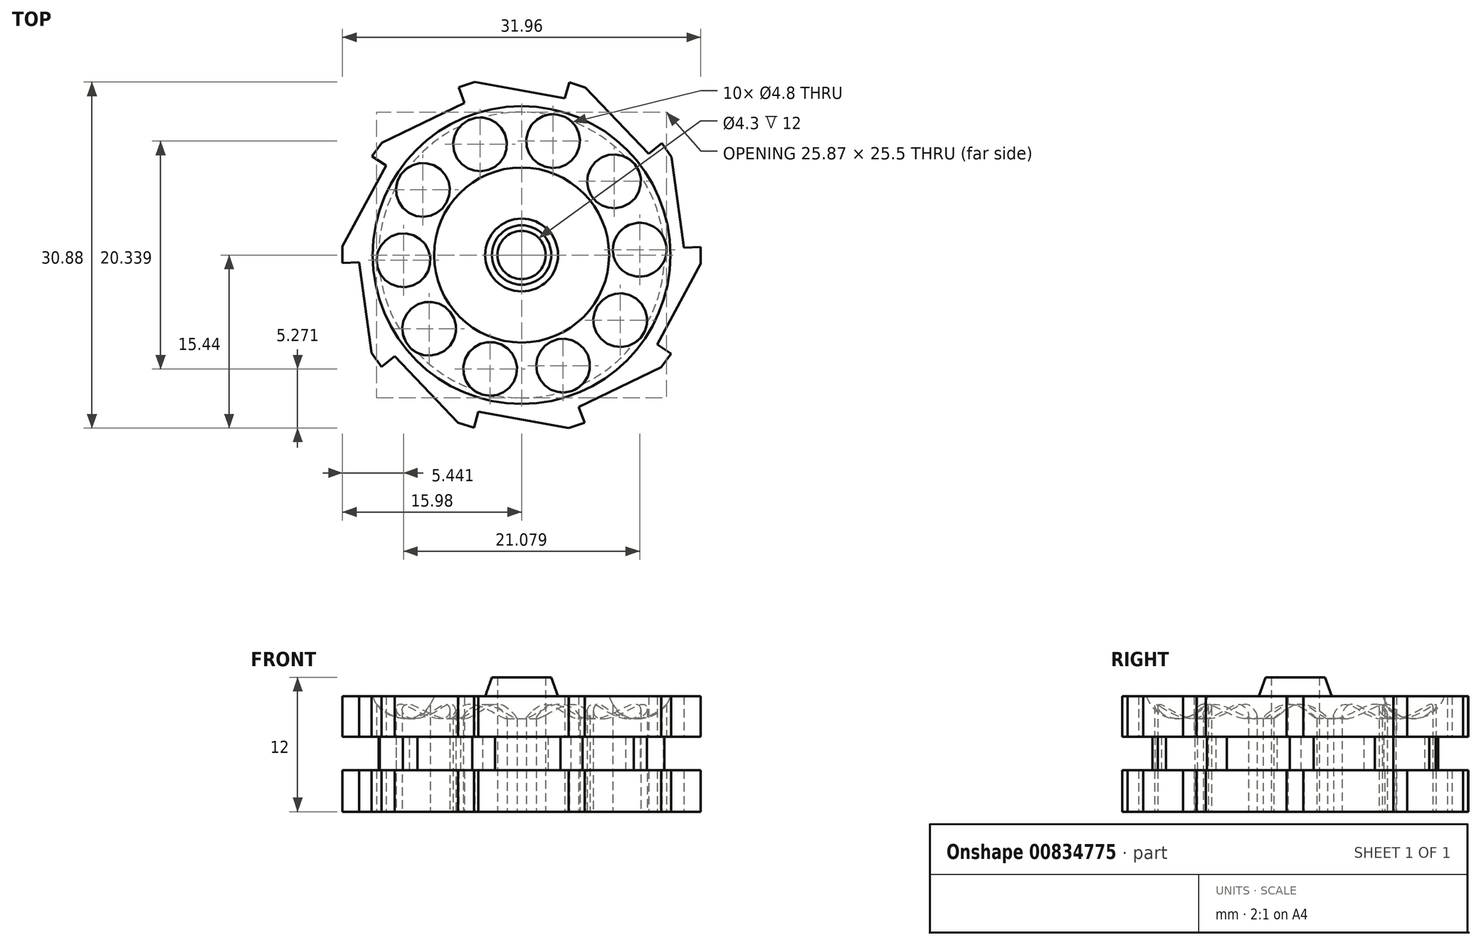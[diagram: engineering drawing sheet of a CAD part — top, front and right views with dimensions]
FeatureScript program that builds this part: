
annotation { "Feature Type Name" : "Feature", "Feature Type Description" : "" }
export const myFeature = defineFeature(function(context is Context, id is Id, definition is map)
    precondition{}
    {
        {
            var Q0;
            Q0=qCreatedBy(makeId("Top.planeOp"),FACE);
            var sketch = newSketch(context, id + "F0", { "sketchPlane" : qUnion([Q0])});
            skCircle(sketch, "E0", {"center": v(0, 0) * mm, "radius": 2.15 * mm});
            skLineSegment(sketch, "E1", {"start": v(-4.2, 15.44) * mm, "end": v(-5.62, 14.98) * mm});
            skLineSegment(sketch, "E2", {"start": v(-5.62, 14.98) * mm, "end": v(-5.1, 13.58) * mm});
            skLineSegment(sketch, "E3", {"start": v(-4.2, 15.44) * mm, "end": v(3.86, 13.98) * mm});
            skLineSegment(sketch, "E4.1.0", {"start": v(-13.35, 8.82) * mm, "end": v(-12.1, 7.99) * mm});
            skLineSegment(sketch, "E4.1.1", {"start": v(-12.47, 10.03) * mm, "end": v(-13.35, 8.82) * mm});
            skLineSegment(sketch, "E4.1.2", {"start": v(-12.47, 10.03) * mm, "end": v(-5.1, 13.58) * mm});
            skLineSegment(sketch, "E4.2.0", {"start": v(-15.98, -0.72) * mm, "end": v(-14.49, -0.65) * mm});
            skLineSegment(sketch, "E4.2.1", {"start": v(-15.98, 0.78) * mm, "end": v(-15.98, -0.72) * mm});
            skLineSegment(sketch, "E4.2.2", {"start": v(-15.98, 0.78) * mm, "end": v(-12.1, 7.99) * mm});
            skLineSegment(sketch, "E4.3.0", {"start": v(-12.51, -9.97) * mm, "end": v(-11.34, -9.04) * mm});
            skLineSegment(sketch, "E4.3.1", {"start": v(-13.39, -8.76) * mm, "end": v(-12.51, -9.97) * mm});
            skLineSegment(sketch, "E4.3.2", {"start": v(-13.39, -8.76) * mm, "end": v(-14.49, -0.65) * mm});
            skLineSegment(sketch, "E4.4.0", {"start": v(-4.26, -15.42) * mm, "end": v(-3.86, -13.98) * mm});
            skLineSegment(sketch, "E4.4.1", {"start": v(-5.68, -14.96) * mm, "end": v(-4.26, -15.42) * mm});
            skLineSegment(sketch, "E4.4.2", {"start": v(-5.68, -14.96) * mm, "end": v(-11.34, -9.04) * mm});
            skLineSegment(sketch, "E4.5.0", {"start": v(5.62, -14.98) * mm, "end": v(5.1, -13.58) * mm});
            skLineSegment(sketch, "E4.5.1", {"start": v(4.2, -15.44) * mm, "end": v(5.62, -14.98) * mm});
            skLineSegment(sketch, "E4.5.2", {"start": v(4.2, -15.44) * mm, "end": v(-3.86, -13.98) * mm});
            skLineSegment(sketch, "E4.6.0", {"start": v(13.35, -8.82) * mm, "end": v(12.1, -7.99) * mm});
            skLineSegment(sketch, "E4.6.1", {"start": v(12.47, -10.03) * mm, "end": v(13.35, -8.82) * mm});
            skLineSegment(sketch, "E4.6.2", {"start": v(12.47, -10.03) * mm, "end": v(5.1, -13.58) * mm});
            skLineSegment(sketch, "E4.7.0", {"start": v(15.98, 0.72) * mm, "end": v(14.49, 0.65) * mm});
            skLineSegment(sketch, "E4.7.1", {"start": v(15.98, -0.78) * mm, "end": v(15.98, 0.72) * mm});
            skLineSegment(sketch, "E4.7.2", {"start": v(15.98, -0.78) * mm, "end": v(12.1, -7.99) * mm});
            skLineSegment(sketch, "E4.8.0", {"start": v(12.51, 9.97) * mm, "end": v(11.34, 9.04) * mm});
            skLineSegment(sketch, "E4.8.1", {"start": v(13.39, 8.76) * mm, "end": v(12.51, 9.97) * mm});
            skLineSegment(sketch, "E4.8.2", {"start": v(13.39, 8.76) * mm, "end": v(14.49, 0.65) * mm});
            skLineSegment(sketch, "E4.9.0", {"start": v(4.26, 15.42) * mm, "end": v(3.86, 13.98) * mm});
            skLineSegment(sketch, "E4.9.1", {"start": v(5.68, 14.96) * mm, "end": v(4.26, 15.42) * mm});
            skLineSegment(sketch, "E4.9.2", {"start": v(5.68, 14.96) * mm, "end": v(11.34, 9.04) * mm});
            skLineSegment(sketch, "E5", {"start": v(0, 0) * mm, "end": v(-3.7, 9.88) * mm, "construction": true});
            skCircle(sketch, "E6", {"center": v(-3.7, 9.88) * mm, "radius": 2.4 * mm});
            skCircle(sketch, "E7.1.0", {"center": v(-8.8, 5.81) * mm, "radius": 2.4 * mm});
            skCircle(sketch, "E7.2.0", {"center": v(-10.54, -0.47) * mm, "radius": 2.4 * mm});
            skCircle(sketch, "E7.3.0", {"center": v(-8.25, -6.58) * mm, "radius": 2.4 * mm});
            skCircle(sketch, "E7.4.0", {"center": v(-2.8, -10.17) * mm, "radius": 2.4 * mm});
            skCircle(sketch, "E7.5.0", {"center": v(3.7, -9.88) * mm, "radius": 2.4 * mm});
            skCircle(sketch, "E7.6.0", {"center": v(8.8, -5.81) * mm, "radius": 2.4 * mm});
            skCircle(sketch, "E7.7.0", {"center": v(10.54, 0.47) * mm, "radius": 2.4 * mm});
            skCircle(sketch, "E7.8.0", {"center": v(8.25, 6.58) * mm, "radius": 2.4 * mm});
            skCircle(sketch, "E7.9.0", {"center": v(2.8, 10.17) * mm, "radius": 2.4 * mm});
            skCircle(sketch, "E8", {"center": v(0, 0) * mm, "radius": 3.25 * mm});
            skSolve(sketch);
        }
        {
            var Q0;
            Q0=makeQuery(id+"F0.imprint","IMPRINT",FACE,{"disambiguationData":[TD([[makeQuery(id+"F0.imprint","IMPRINT",EDGE,{"derivedFrom":sQuery(id+"F0.wireOp",EDGE,"E1")}),1.0]])]});
            var Q1;
            Q1=makeQuery(id+"F0.imprint","IMPRINT",FACE,{"disambiguationData":[TD([[makeQuery(id+"F0.imprint","IMPRINT",EDGE,{"derivedFrom":sQuery(id+"F0.wireOp",EDGE,"E0")}),-1.0]])]});
            extrude(context, id + "F1", {"entities" : qUnion([Q0, Q1]), "depth" : 10.3 * mm, "offsetDistance" : 25 * mm});
        }
        {
            var Q0;
            Q0=qCreatedBy(makeId("Front.planeOp"),FACE);
            var sketch = newSketch(context, id + "F2", { "sketchPlane" : qUnion([Q0])});
            skLineSegment(sketch, "E9", {"start": v(0, 0) * mm, "end": v(0, 3.7) * mm, "construction": true});
            skLineSegment(sketch, "E10", {"start": v(0, 3.7) * mm, "end": v(12.75, 3.7) * mm, "construction": true});
            skLineSegment(sketch, "E11.bottom", {"start": v(12.75, 3.7) * mm, "end": v(17.75, 3.7) * mm});
            skLineSegment(sketch, "E11.top", {"start": v(12.75, 6.7) * mm, "end": v(17.75, 6.7) * mm});
            skLineSegment(sketch, "E11.left", {"start": v(12.75, 3.7) * mm, "end": v(12.75, 6.7) * mm});
            skLineSegment(sketch, "E11.right", {"start": v(17.75, 3.7) * mm, "end": v(17.75, 6.7) * mm});
            skSolve(sketch);
        }
        {
            var Q0;
            Q0=makeQuery(id+"F2.imprint","IMPRINT",FACE,{"disambiguationData":[TD([[makeQuery(id+"F2.imprint","IMPRINT",EDGE,{"derivedFrom":sQuery(id+"F2.wireOp",EDGE,"E11.bottom")}),1.0]])]});
            var Q1;
            Q1=sQuery(id+"F2.wireOp",EDGE,"E9");
            revolve(context, id + "F3", {"surfaceOperationType" : NewSurfaceOperationType.NEW, "entities" : qUnion([Q0]), "axis" : qUnion([Q1]), "revolveType" : RevolveType.FULL});
        }
        {
            var Q0;
            Q0=makeQuery(id+"F3.opRevolve","SWEPT_BODY",BODY,{"disambiguationData":[OSD([sQuery(id+"F2.wireOp",EDGE,"E11.bottom"),sQuery(id+"F2.wireOp",EDGE,"E11.top"),sQuery(id+"F2.wireOp",EDGE,"E11.left"),sQuery(id+"F2.wireOp",EDGE,"E11.right")])]});
            var Q1;
            Q1=makeQuery(id+"F1.opExtrude","SWEPT_BODY",BODY,{"disambiguationData":[OSD([sQuery(id+"F0.wireOp",EDGE,"E0"),sQuery(id+"F0.wireOp",EDGE,"E1"),sQuery(id+"F0.wireOp",EDGE,"E2"),sQuery(id+"F0.wireOp",EDGE,"E3"),sQuery(id+"F0.wireOp",EDGE,"E4.1.0"),sQuery(id+"F0.wireOp",EDGE,"E4.1.1"),sQuery(id+"F0.wireOp",EDGE,"E4.1.2"),sQuery(id+"F0.wireOp",EDGE,"E4.2.0"),sQuery(id+"F0.wireOp",EDGE,"E4.2.1"),sQuery(id+"F0.wireOp",EDGE,"E4.2.2"),sQuery(id+"F0.wireOp",EDGE,"E4.3.0"),sQuery(id+"F0.wireOp",EDGE,"E4.3.1"),sQuery(id+"F0.wireOp",EDGE,"E4.3.2"),sQuery(id+"F0.wireOp",EDGE,"E4.4.0"),sQuery(id+"F0.wireOp",EDGE,"E4.4.1"),sQuery(id+"F0.wireOp",EDGE,"E4.4.2"),sQuery(id+"F0.wireOp",EDGE,"E4.5.0"),sQuery(id+"F0.wireOp",EDGE,"E4.5.1"),sQuery(id+"F0.wireOp",EDGE,"E4.5.2"),sQuery(id+"F0.wireOp",EDGE,"E4.6.0"),sQuery(id+"F0.wireOp",EDGE,"E4.6.1"),sQuery(id+"F0.wireOp",EDGE,"E4.6.2"),sQuery(id+"F0.wireOp",EDGE,"E4.7.0"),sQuery(id+"F0.wireOp",EDGE,"E4.7.1"),sQuery(id+"F0.wireOp",EDGE,"E4.7.2"),sQuery(id+"F0.wireOp",EDGE,"E4.8.0"),sQuery(id+"F0.wireOp",EDGE,"E4.8.1"),sQuery(id+"F0.wireOp",EDGE,"E4.8.2"),sQuery(id+"F0.wireOp",EDGE,"E4.9.0"),sQuery(id+"F0.wireOp",EDGE,"E4.9.1"),sQuery(id+"F0.wireOp",EDGE,"E4.9.2"),sQuery(id+"F0.wireOp",EDGE,"E6"),sQuery(id+"F0.wireOp",EDGE,"E7.1.0"),sQuery(id+"F0.wireOp",EDGE,"E7.2.0"),sQuery(id+"F0.wireOp",EDGE,"E7.3.0"),sQuery(id+"F0.wireOp",EDGE,"E7.4.0"),sQuery(id+"F0.wireOp",EDGE,"E7.5.0"),sQuery(id+"F0.wireOp",EDGE,"E7.6.0"),sQuery(id+"F0.wireOp",EDGE,"E7.7.0"),sQuery(id+"F0.wireOp",EDGE,"E7.8.0"),sQuery(id+"F0.wireOp",EDGE,"E7.9.0")])]});
            booleanBodies(context, id + "F4", {"operationType" : BooleanOperationType.SUBTRACTION, "tools" : qUnion([Q0]), "targets" : qUnion([Q1])});
        }
        {
            var Q0;
            Q0=qCreatedBy(makeId("Right.planeOp"),FACE);
            var sketch = newSketch(context, id + "F5", { "sketchPlane" : qUnion([Q0])});
            skLineSegment(sketch, "E12", {"start": v(0, 0) * mm, "end": v(0, 10.3) * mm, "construction": true});
            skLineSegment(sketch, "E13", {"start": v(0, 10.3) * mm, "end": v(3.25, 10.3) * mm});
            skLineSegment(sketch, "E14", {"start": v(3.25, 10.3) * mm, "end": v(2.65, 12) * mm});
            skLineSegment(sketch, "E15", {"start": v(2.65, 12) * mm, "end": v(2.65, 10.3) * mm});
            skLineSegment(sketch, "E16.bottom", {"start": v(2.65, 12) * mm, "end": v(2.15, 12) * mm});
            skLineSegment(sketch, "E16.top", {"start": v(2.65, 10.3) * mm, "end": v(2.15, 10.3) * mm, "construction": true});
            skLineSegment(sketch, "E16.left", {"start": v(2.65, 12) * mm, "end": v(2.65, 10.3) * mm, "construction": true});
            skLineSegment(sketch, "E16.right", {"start": v(2.15, 12) * mm, "end": v(2.15, 10.3) * mm});
            skSolve(sketch);
        }
        {
            var Q0;
            {var subQ0=sQuery(id+"F5.wireOp",EDGE,"E15");Q0=makeQuery(id+"F5.imprint","IMPRINT",FACE,{"disambiguationData":[TD([[makeQuery(id+"F5.imprint","IMPRINT",EDGE,{"derivedFrom":subQ0}),-1.0]])]});}
            var Q1;
            {var subQ0=sQuery(id+"F5.wireOp",EDGE,"E14");Q1=makeQuery(id+"F5.imprint","IMPRINT",FACE,{"disambiguationData":[TD([[makeQuery(id+"F5.imprint","IMPRINT",EDGE,{"derivedFrom":subQ0}),1.0]])]});}
            var Q2;
            Q2=sQuery(id+"F5.wireOp",EDGE,"E12");
            revolve(context, id + "F6", {"operationType" : NewBodyOperationType.ADD, "surfaceOperationType" : NewSurfaceOperationType.NEW, "entities" : qUnion([Q0, Q1]), "axis" : qUnion([Q2]), "revolveType" : RevolveType.FULL});
        }
        {
            var Q0;
            Q0=qCreatedBy(makeId("Front.planeOp"),FACE);
            var sketch = newSketch(context, id + "F7", { "sketchPlane" : qUnion([Q0])});
            skLineSegment(sketch, "E17", {"start": v(0, 0) * mm, "end": v(0, 11.18) * mm, "construction": true});
            skLineSegment(sketch, "E18", {"start": v(0, 11.18) * mm, "end": v(10.55, 11.18) * mm, "construction": true});
            skCircle(sketch, "E19", {"center": v(10.55, 11.18) * mm, "radius": 2.88 * mm});
            skSolve(sketch);
        }
        {
            var Q0;
            Q0=makeQuery(id+"F7.imprint","IMPRINT",FACE,{"disambiguationData":[TD([[makeQuery(id+"F7.imprint","IMPRINT",EDGE,{"derivedFrom":sQuery(id+"F7.wireOp",EDGE,"E19")}),1.0]])]});
            var Q1;
            Q1=sQuery(id+"F7.wireOp",EDGE,"E17");
            revolve(context, id + "F8", {"operationType" : NewBodyOperationType.REMOVE, "surfaceOperationType" : NewSurfaceOperationType.NEW, "entities" : qUnion([Q0]), "axis" : qUnion([Q1]), "revolveType" : RevolveType.FULL, "oppositeDirection" : true});
        }
    });
